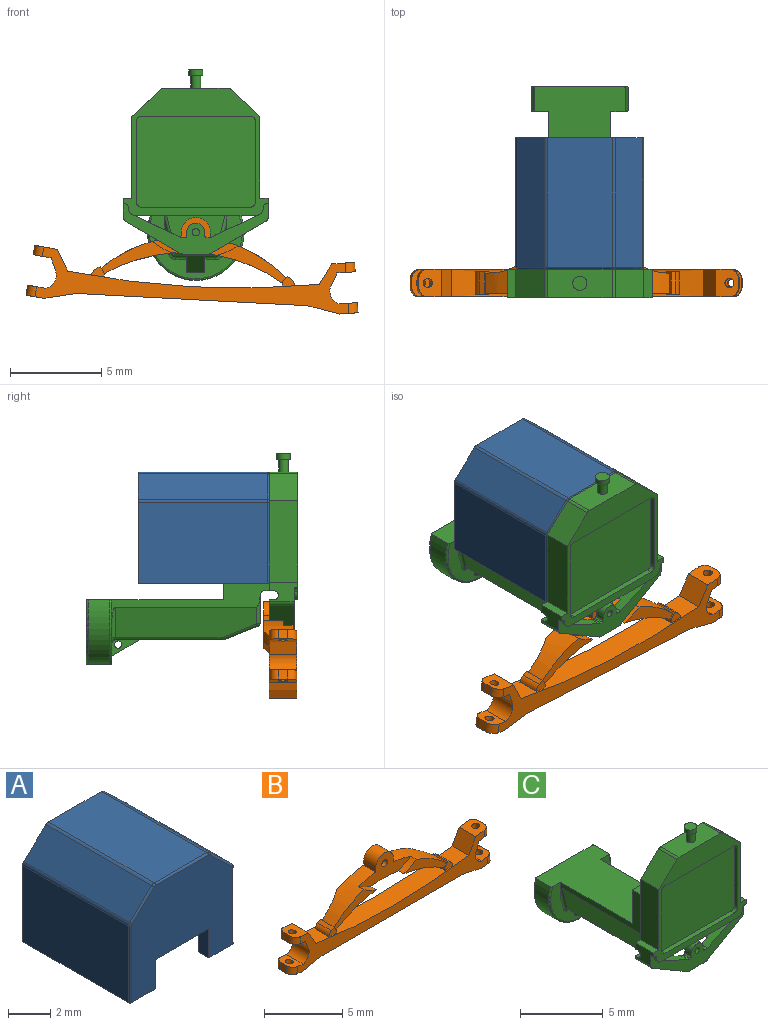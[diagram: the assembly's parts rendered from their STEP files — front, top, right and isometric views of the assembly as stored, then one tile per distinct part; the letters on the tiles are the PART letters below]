
ASSEMBLY  parts=3 mates=4
PART A: 31 faces, bbox 7x7.2x6.1 mm
  f0: plane 7.1x4.44mm, normal (-1,0,0), area 31.5mm2, adj f2,f17,f21,f22
  f1: plane 7.1x4.44mm, normal (1,0,0), area 31.5mm2, adj f2,f16,f18,f30
  f2: plane 7x6.1mm, normal (0,1,0), area 12.1mm2, adj f0,f1,f7,f8,f10,f11,f12,f13
  f3: plane 1.7x0.7mm, normal (1,0,0), area 1.2mm2, adj f5,f6,f9,f17
  f4: plane 1.7x0.7mm, normal (-1,0,0), area 1.2mm2, adj f5,f6,f9,f16
  f5: plane 6.8x6mm, normal (0,-1,0), area 32.3mm2, adj f3,f4,f9,f16,f17,f22,f23,f24
  f6: plane 5.5x5.35mm, normal (0,1,0), area 22mm2, adj f3,f4,f7,f8,f9,f13,f14,f15
  f7: plane 6.5x4.23mm, normal (1,0,0), area 27.5mm2, adj f2,f6,f13,f17
  f8: plane 6.5x4.23mm, normal (-1,0,0), area 27.5mm2, adj f2,f6,f15,f16
  f9: plane 3.6x0.7mm, normal (0,0,-1), area 2.5mm2, adj f3,f4,f5,f6
  f10: plane 7.1x1.48mm, normal (0.69,0,0.72), area 14.5mm2, adj f2,f18,f19,f28
  f11: plane 7.1x3.54mm, normal (0,0,1), area 25.1mm2, adj f2,f19,f20,f26
  f12: plane 7.1x1.48mm, normal (-0.69,0,0.72), area 14.5mm2, adj f2,f20,f21,f24
  f13: plane 6.5x1.18mm, normal (0.69,0,-0.72), area 10.6mm2, adj f2,f6,f7,f14
  f14: plane 6.5x3.14mm, normal (0,0,-1), area 20.4mm2, adj f2,f6,f13,f15
  f15: plane 6.5x1.18mm, normal (-0.69,0,-0.72), area 10.6mm2, adj f2,f6,f8,f14
  f16: plane 7.2x1.7mm, normal (0,0,-1), area 6.1mm2, adj f1,f2,f4,f5,f6,f8,f30
  f17: plane 7.2x1.7mm, normal (0,0,-1), area 6.1mm2, adj f0,f2,f3,f5,f6,f7,f22
  f18: cylinder r=0.25mm len=7.1mm, axis (0,-1,0), area 1.4mm2, adj f1,f2,f10,f29
  f19: cylinder r=0.25mm len=7.1mm, axis (0,1,0), area 1.3mm2, adj f2,f10,f11,f27
  f20: cylinder r=0.25mm len=7.1mm, axis (0,1,0), area 1.3mm2, adj f2,f11,f12,f25
  f21: cylinder r=0.25mm len=7.1mm, axis (0,1,0), area 1.4mm2, adj f0,f2,f12,f23
  f22: cylinder r=0.1mm len=4.44mm, axis (0,0,1), area 0.7mm2, adj f0,f5,f17,f23
  f23: torus R=0.15mm, axis (0,-1,0), area 0mm2, adj f5,f21,f22,f24
  f24: cylinder r=0.1mm len=1.55mm, axis (0.72,0,0.69), area 0.3mm2, adj f5,f12,f23,f25
  f25: torus R=0.15mm, axis (0,-1,0), area 0mm2, adj f5,f20,f24,f26
  f26: cylinder r=0.1mm len=3.54mm, axis (1,0,0), area 0.6mm2, adj f5,f11,f25,f27
  f27: torus R=0.15mm, axis (0,-1,0), area 0mm2, adj f5,f19,f26,f28
  f28: cylinder r=0.1mm len=1.55mm, axis (0.72,0,-0.69), area 0.3mm2, adj f5,f10,f27,f29
  f29: torus R=0.15mm, axis (0,-1,0), area 0mm2, adj f5,f18,f28,f30
  f30: cylinder r=0.1mm len=4.44mm, axis (0,0,-1), area 0.7mm2, adj f1,f5,f16,f29
PART B: 69 faces, bbox 18.2x1.8x4.9 mm
  f0: plane 0.45x0.31mm, normal (0,1,0), area 0.1mm2, adj f6,f46,f51,f59
  f1: plane 1.1x0.29mm, normal (1,0,0), area 0.3mm2, adj f5,f6,f56,f57
  f2: plane 1.1x0.29mm, normal (-1,0,0), area 0.3mm2, adj f3,f5,f56,f57
  f3: cylinder r=7.46mm len=4.27mm, axis (0,1,0), area 6mm2, adj f2,f4,f42,f53,f55,f56,f57,f60
  f4: plane 3.82x1.9mm, normal (0,-1,0), area 2.1mm2, adj f3,f42,f51,f55
  f5: cylinder r=0.8mm len=1.6mm, axis (0,1,0), area 2.8mm2, adj f1,f2,f56,f57
  f6: cylinder r=7.46mm len=4.27mm, axis (0,1,0), area 6mm2, adj f0,f1,f46,f52,f54,f56,f57,f59
  f7: cylinder r=47.86mm len=13.8mm, axis (0,1,0), area 19mm2, adj f10,f11,f16,f26,f40,f41,f43,f44
  f8: plane 0.51x0.5mm, normal (-0.99,0,0.12), area 0.3mm2, adj f17,f28,f30,f32
  f9: plane 0.51x0.5mm, normal (0.99,0,0.12), area 0.3mm2, adj f12,f14,f25,f35
  f10: plane 17.24x2.81mm, normal (0,-1,0), area 16.8mm2, adj f7,f14,f15,f16,f17,f19,f20,f21
  f11: plane 17.24x2.81mm, normal (0,1,0), area 16.6mm2, adj f7,f12,f13,f16,f17,f19,f20,f21
  f12: cylinder r=0.5mm len=0.57mm, axis (-0.12,0,0.99), area 0.4mm2, adj f9,f11,f25,f35
  f13: cylinder r=0.5mm len=0.61mm, axis (-0.12,0,-0.99), area 0.4mm2, adj f11,f18,f19,f33
  f14: cylinder r=0.5mm len=0.57mm, axis (0.12,0,-0.99), area 0.4mm2, adj f9,f10,f25,f35
  f15: cylinder r=0.5mm len=0.61mm, axis (0.12,0,0.99), area 0.4mm2, adj f10,f18,f19,f33
  f16: plane 1.5x1.16mm, normal (0.88,0,0.48), area 2mm2, adj f7,f10,f11,f17
  f17: plane 1.5x1.24mm, normal (0.12,0,0.99), area 1.6mm2, adj f8,f10,f11,f16,f28,f30,f62
  f18: plane 0.55x0.5mm, normal (-0.99,0,0.12), area 0.3mm2, adj f13,f15,f19,f33
  f19: plane 1.5x0.99mm, normal (-0.12,0,-0.99), area 1.2mm2, adj f10,f11,f13,f15,f18,f20,f61
  f20: plane 1.78x1.5mm, normal (0.2,0,-0.98), area 2.7mm2, adj f10,f11,f19,f21
  f21: plane 12.7x1.5mm, normal (0,0,-1), area 19mm2, adj f10,f11,f20,f22
  f22: plane 1.78x1.5mm, normal (-0.2,0,-0.98), area 2.7mm2, adj f10,f11,f21,f23
  f23: plane 1.5x0.99mm, normal (0.12,0,-0.99), area 1.2mm2, adj f10,f11,f22,f24,f27,f29,f63
  f24: plane 0.55x0.5mm, normal (0.99,0,0.12), area 0.3mm2, adj f23,f27,f29,f36
  f25: plane 1.5x1.24mm, normal (-0.12,0,0.99), area 1.6mm2, adj f9,f10,f11,f12,f14,f26,f64
  f26: plane 1.5x1.16mm, normal (-0.88,0,0.48), area 2mm2, adj f7,f10,f11,f25
  f27: cylinder r=0.5mm len=0.61mm, axis (-0.12,0,0.99), area 0.4mm2, adj f11,f23,f24,f36
  f28: cylinder r=0.5mm len=0.57mm, axis (-0.12,0,-0.99), area 0.4mm2, adj f8,f11,f17,f32
  f29: cylinder r=0.5mm len=0.61mm, axis (0.12,0,-0.99), area 0.4mm2, adj f10,f23,f24,f36
  f30: cylinder r=0.5mm len=0.57mm, axis (0.12,0,0.99), area 0.4mm2, adj f8,f10,f17,f32
  f31: plane 1.5x0.68mm, normal (-0.93,0,-0.38), area 1.1mm2, adj f10,f11,f32,f37
  f32: plane 1.5x0.99mm, normal (-0.12,0,-0.99), area 1.2mm2, adj f8,f10,f11,f28,f30,f31,f62
  f33: plane 1.5x0.99mm, normal (0.12,0,0.99), area 1.2mm2, adj f10,f11,f13,f15,f18,f37,f61
  f34: plane 1.5x0.68mm, normal (0.93,0,-0.38), area 1.1mm2, adj f10,f11,f35,f38
  f35: plane 1.5x0.99mm, normal (0.12,0,-0.99), area 1.2mm2, adj f9,f10,f11,f12,f14,f34,f64
  f36: plane 1.5x0.99mm, normal (-0.12,0,0.99), area 1.2mm2, adj f10,f11,f24,f27,f29,f38,f63
  f37: cylinder r=0.75mm len=1.5mm, axis (0,-1,0), area 1.9mm2, adj f10,f11,f31,f33
  f38: cylinder r=0.75mm len=1.5mm, axis (0,-1,0), area 1.9mm2, adj f10,f11,f34,f36
  f39: plane 1.25x0.25mm, normal (-0.55,0,0.83), area 0.4mm2, adj f40,f42,f43,f44
  f40: cylinder r=0.5mm len=1.25mm, axis (0,1,0), area 0.5mm2, adj f7,f39,f43,f44
  f41: plane 1.25x0.22mm, normal (0.99,0,-0.11), area 0.3mm2, adj f7,f42,f43,f44,f51
  f42: plane 1.25x0.38mm, normal (0.83,0,0.55), area 0.2mm2, adj f3,f4,f39,f41,f43,f44,f53
  f43: plane 0.72x0.6mm, normal (0,-1,0), area 0.3mm2, adj f7,f39,f40,f41,f42
  f44: plane 0.72x0.6mm, normal (0,1,0), area 0.3mm2, adj f7,f39,f40,f41,f42
  f45: plane 1.25x0.25mm, normal (0.55,0,0.83), area 0.4mm2, adj f46,f48,f49,f50
  f46: plane 1.25x0.38mm, normal (-0.83,0,0.55), area 0.2mm2, adj f0,f6,f45,f47,f49,f50,f52
  f47: plane 1.25x0.22mm, normal (-0.99,0,-0.11), area 0.3mm2, adj f7,f46,f49,f50,f51
  f48: cylinder r=0.5mm len=1.25mm, axis (0,1,0), area 0.5mm2, adj f7,f45,f49,f50
  f49: plane 0.72x0.6mm, normal (0,-1,0), area 0.3mm2, adj f7,f45,f46,f47,f48
  f50: plane 0.72x0.6mm, normal (0,1,0), area 0.3mm2, adj f7,f45,f46,f47,f48
  f51: cylinder r=9.12mm len=9.75mm, axis (0,1,0), area 13.8mm2, adj f0,f4,f41,f47,f52,f53,f54,f55
  f52: plane 3.82x1.9mm, normal (0,-1,0), area 2.1mm2, adj f6,f46,f51,f54
  f53: plane 0.45x0.31mm, normal (0,1,0), area 0.1mm2, adj f3,f42,f51,f60
  f54: cylinder r=4mm len=1.11mm, axis (0,-1,0), area 0.6mm2, adj f6,f51,f52,f56
  f55: cylinder r=4mm len=1.11mm, axis (0,-1,0), area 0.6mm2, adj f3,f4,f51,f56
  f56: plane 4.71x2mm, normal (0,-1,0), area 4.4mm2, adj f1,f2,f3,f5,f6,f51,f54,f55
  f57: plane 6.45x2.42mm, normal (0,1,0), area 6.4mm2, adj f1,f2,f3,f5,f6,f51,f58,f59
  f58: cylinder r=0.25mm len=1.1mm, axis (0,-1,0), area 1.7mm2, adj f56,f57
  f59: cylinder r=4mm len=2.12mm, axis (-0.33,0,-0.94), area 1.1mm2, adj f0,f6,f51,f57
  f60: cylinder r=4mm len=2.12mm, axis (0.33,0,-0.94), area 1.1mm2, adj f3,f51,f53,f57
  f61: cylinder r=0.25mm len=0.61mm, axis (0.12,0,0.99), area 0.9mm2, adj f19,f33
  f62: cylinder r=0.25mm len=0.57mm, axis (0.12,0,0.99), area 0.8mm2, adj f17,f32
  f63: cylinder r=0.25mm len=0.61mm, axis (-0.12,0,0.99), area 0.9mm2, adj f23,f36
  f64: cylinder r=0.25mm len=0.57mm, axis (-0.12,0,0.99), area 0.8mm2, adj f25,f35
  f65: cylinder r=0.2mm len=1mm, axis (0,1,0), area 1.3mm2, adj f11,f66
  f66: plane 0.4x0.4mm, normal (0,1,0), area 0.1mm2, adj f65
  f67: cylinder r=0.2mm len=1mm, axis (0,1,0), area 1.3mm2, adj f11,f68
  f68: plane 0.4x0.4mm, normal (0,1,0), area 0.1mm2, adj f67
PART C: 115 faces, bbox 8x11.6x11.8 mm
  f0: plane 5.1x3.45mm, normal (0,-1,0), area 6.2mm2, adj f6,f7,f62,f81,f83,f84,f85,f94
  f1: plane 7.94x6.5mm, normal (0,1,0), area 36.6mm2, adj f3,f4,f6,f7,f10,f23,f24,f25
  f2: plane 2.57x1.14mm, normal (0,1,0), area 1.2mm2, adj f4,f12,f47,f52,f54,f68,f72,f107
  f3: plane 1.56x1.06mm, normal (1,0,0), area 1.3mm2, adj f1,f11,f20,f28,f44,f50,f69,f71
  f4: plane 1.56x1.06mm, normal (-1,0,0), area 1.3mm2, adj f1,f2,f19,f28,f45,f50,f69,f70
  f5: plane 6.5x0.99mm, normal (0,0,-1), area 6mm2, adj f9,f28,f46,f56,f57,f75,f77
  f6: plane 8.65x3.74mm, normal (1,0,0), area 9.3mm2, adj f0,f1,f10,f59,f62,f63,f69,f74
  f7: plane 8.65x3.74mm, normal (-1,0,0), area 9.3mm2, adj f0,f1,f10,f61,f62,f63,f69,f74
  f8: plane 2.41x1.36mm, normal (-0.42,0,0.91), area 3.1mm2, adj f11,f50,f53,f55,f67,f111
  f9: cylinder r=0.45mm len=0.99mm, axis (0,-1,0), area 0.2mm2, adj f5,f22,f28,f50,f67,f76
  f10: plane 3.4x2.5mm, normal (0,0,1), area 8.5mm2, adj f1,f6,f7,f63
  f11: plane 2.57x1.14mm, normal (0,1,0), area 1.2mm2, adj f3,f8,f49,f51,f55,f67,f73,f108
  f12: plane 2.41x1.36mm, normal (0.42,0,0.91), area 3.1mm2, adj f2,f50,f53,f54,f68,f112
  f13: cylinder r=0.5mm len=1mm, axis (0,-1,0), area 0.9mm2, adj f17,f18,f50,f53
  f14: cylinder r=0.2mm len=0.56mm, axis (0,-1,0), area 0.7mm2, adj f50,f53
  f15: plane 0.56x0.09mm, normal (0,0,1), area 0.1mm2, adj f50,f53,f112,f113
  f16: plane 0.56x0.09mm, normal (0,0,1), area 0.1mm2, adj f50,f53,f111,f114
  f17: plane 0.56x0.2mm, normal (-1,0,0), area 0.1mm2, adj f13,f50,f53,f113
  f18: plane 0.56x0.2mm, normal (1,0,0), area 0.1mm2, adj f13,f50,f53,f114
  f19: plane 0.2x0.05mm, normal (0,0,-1), area 0mm2, adj f4,f21,f28,f50
  f20: plane 0.2x0.05mm, normal (0,0,-1), area 0mm2, adj f3,f22,f28,f50
  f21: cylinder r=0.22mm len=0.22mm, axis (0,-1,0), area 0.1mm2, adj f19,f28,f46,f50
  f22: cylinder r=0.22mm len=0.22mm, axis (0,-1,0), area 0.1mm2, adj f9,f20,f28,f50
  f23: plane 4.48x1.56mm, normal (-1,0,0), area 7mm2, adj f1,f27,f28,f45
  f24: plane 4.48x1.56mm, normal (1,0,0), area 7mm2, adj f1,f25,f28,f44
  f25: plane 1.56x1.56mm, normal (0.69,0,0.72), area 3.4mm2, adj f1,f24,f28,f42
  f26: plane 3.54x1.56mm, normal (0,0,1), area 5.3mm2, adj f1,f28,f38,f42,f43
  f27: plane 1.56x1.56mm, normal (-0.69,0,0.72), area 3.4mm2, adj f1,f23,f28,f43
  f28: plane 7.94x7mm, normal (0,-1,0), area 14.3mm2, adj f3,f4,f5,f9,f19,f20,f21,f22
  f29: plane 4.4x0.3mm, normal (1,0,0), area 1.3mm2, adj f28,f33,f34,f37
  f30: plane 5.94x0.3mm, normal (0,0,1), area 1.8mm2, adj f28,f33,f34,f35
  f31: plane 4.4x0.3mm, normal (-1,0,0), area 1.3mm2, adj f28,f33,f35,f36
  f32: plane 5.94x0.3mm, normal (0,0,-1), area 1.8mm2, adj f28,f33,f36,f37
  f33: plane 6.54x5mm, normal (0,-1,0), area 32.6mm2, adj f29,f30,f31,f32,f34,f35,f36,f37
  f34: cylinder r=0.3mm len=0.3mm, axis (0,1,0), area 0.1mm2, adj f28,f29,f30,f33
  f35: cylinder r=0.3mm len=0.3mm, axis (0,-1,0), area 0.1mm2, adj f28,f30,f31,f33
  f36: cylinder r=0.3mm len=0.3mm, axis (0,1,0), area 0.1mm2, adj f28,f31,f32,f33
  f37: cylinder r=0.3mm len=0.3mm, axis (0,-1,0), area 0.1mm2, adj f28,f29,f32,f33
  f38: cylinder r=0.28mm len=0.7mm, axis (0,0,-1), area 1.2mm2, adj f26,f41
  f39: cylinder r=0.39mm len=0.78mm, axis (0,0,-1), area 0.7mm2, adj f40,f41
  f40: plane 0.78x0.78mm, normal (0,0,1), area 0.5mm2, adj f39
  f41: plane 0.78x0.78mm, normal (0,0,-1), area 0.2mm2, adj f38,f39
  f42: cylinder r=0.25mm len=1.56mm, axis (0,1,0), area 0.3mm2, adj f1,f25,f26,f28
  f43: cylinder r=0.25mm len=1.56mm, axis (0,1,0), area 0.3mm2, adj f1,f26,f27,f28
  f44: plane 1.56x0.47mm, normal (0,0,1), area 0.7mm2, adj f1,f3,f24,f28
  f45: plane 1.56x0.47mm, normal (0,0,1), area 0.7mm2, adj f1,f4,f23,f28
  f46: cylinder r=0.45mm len=0.99mm, axis (0,-1,0), area 0.2mm2, adj f5,f21,f28,f50,f68,f78
  f47: plane 2.97x1.74mm, normal (-0.51,0,-0.86), area 3.3mm2, adj f2,f50,f52,f53,f107,f109
  f48: plane 1.34x0.56mm, normal (0,0,-1), area 0.8mm2, adj f50,f53,f109,f110
  f49: plane 2.97x1.74mm, normal (0.51,0,-0.86), area 3.3mm2, adj f11,f50,f51,f53,f108,f110
  f50: plane 7.94x2.77mm, normal (0,-1,0), area 6.7mm2, adj f3,f4,f8,f9,f12,f13,f14,f15
  f51: cylinder r=10mm len=1.01mm, axis (0,1,0), area 0.8mm2, adj f11,f49,f53,f55
  f52: cylinder r=10mm len=1.01mm, axis (0,1,0), area 0.8mm2, adj f2,f47,f53,f54
  f53: plane 4.82x1.7mm, normal (0,1,0), area 3.9mm2, adj f8,f12,f13,f14,f15,f16,f17,f18
  f54: cylinder r=1.4mm len=0.8mm, axis (0,1,0), area 0mm2, adj f2,f12,f52,f53
  f55: cylinder r=1.4mm len=0.8mm, axis (0,1,0), area 0mm2, adj f8,f11,f51,f53
  f56: plane 2.14x0.5mm, normal (0,1,0), area 0.7mm2, adj f5,f57
  f57: cylinder r=1.4mm len=2.14mm, axis (0,1,0), area 1mm2, adj f5,f56,f70,f71,f75,f77
  f58: plane 3.31x1.51mm, normal (0,-1,0), area 4.3mm2, adj f64,f74,f87,f90,f99
  f59: plane 7.74x1.65mm, normal (0.97,0,-0.24), area 12.5mm2, adj f6,f99,f101,f103,f104
  f60: plane 5.9x2.19mm, normal (0,0,-1), area 11.6mm2, adj f81,f83,f84,f88,f95,f97,f103,f106
  f61: plane 7.74x1.65mm, normal (-0.97,0,-0.24), area 12.5mm2, adj f7,f90,f92,f94,f95
  f62: plane 7.56x5mm, normal (0,0,1), area 27.8mm2, adj f0,f6,f7,f63,f79,f80,f85,f86
  f63: plane 3.4x2.5mm, normal (0,1,0), area 8.5mm2, adj f6,f7,f10,f62
  f64: cylinder r=0.2mm len=5mm, axis (0,-1,0), area 6.3mm2, adj f58,f65
  f65: plane 0.4x0.4mm, normal (0,-1,0), area 0.1mm2, adj f64
  f66: plane 2.56x1.84mm, normal (0,-0.37,-0.93), area 4.7mm2, adj f87,f88,f92,f101
  f67: plane 1.37x0.19mm, normal (-1,0,0), area 0.1mm2, adj f8,f9,f11,f50,f71,f73,f76
  f68: plane 1.37x0.19mm, normal (1,0,0), area 0.1mm2, adj f2,f12,f46,f50,f70,f72,f78
  f69: plane 7.94x0.5mm, normal (0,0,-1), area 2.8mm2, adj f1,f3,f4,f6,f7,f70,f71,f74
  f70: cylinder r=0.25mm len=3.97mm, axis (1,0,0), area 1.9mm2, adj f4,f57,f68,f69,f72,f77,f78
  f71: cylinder r=0.25mm len=3.97mm, axis (1,0,0), area 1.9mm2, adj f3,f57,f67,f69,f73,f75,f76
  f72: plane 0.7x0.25mm, normal (0,0,1), area 0.2mm2, adj f2,f4,f68,f70
  f73: plane 0.7x0.25mm, normal (0,0,1), area 0.2mm2, adj f3,f11,f67,f71
  f74: cylinder r=0.25mm len=3.4mm, axis (1,0,0), area 1.3mm2, adj f6,f7,f58,f69,f89,f98
  f75: cylinder r=0.1mm len=2.32mm, axis (1,0,0), area 0.5mm2, adj f5,f57,f71,f76
  f76: bspline ~0.22x0.16mm, area 0mm2, adj f9,f67,f71,f75
  f77: cylinder r=0.1mm len=2.32mm, axis (1,0,0), area 0.5mm2, adj f5,f57,f70,f78
  f78: bspline ~0.22x0.16mm, area 0mm2, adj f46,f68,f70,f77
  f79: cylinder r=2.65mm len=5.3mm, axis (0,-1,0), area 12.2mm2, adj f62,f85,f86
  f80: plane 5.1x3.45mm, normal (0,1,0), area 14.7mm2, adj f62,f86
  f81: plane 1.5x1mm, normal (0,-0.51,-0.86), area 1.7mm2, adj f0,f60,f83,f84
  f82: cylinder r=0.2mm len=1mm, axis (-1,0,0), area 1.3mm2, adj f83,f84
  f83: plane 1.5x0.9mm, normal (1,0,0), area 0.5mm2, adj f0,f60,f81,f82,f106
  f84: plane 1.5x0.9mm, normal (-1,0,0), area 0.5mm2, adj f0,f60,f81,f82,f97
  f85: torus R=2.55mm, axis (0,-1,0), area 1.6mm2, adj f0,f62,f79
  f86: torus R=2.55mm, axis (0,-1,0), area 1.6mm2, adj f62,f79,f80
  f87: cylinder r=0.2mm len=2.56mm, axis (1,0,0), area 0.6mm2, adj f58,f66,f91,f100
  f88: cylinder r=0.2mm len=2.19mm, axis (-1,0,0), area 0.2mm2, adj f60,f66,f93,f102
  f89: bspline ~0.26x0.26mm, area 0mm2, adj f7,f74,f90
  f90: cylinder r=0.2mm len=1.56mm, axis (-0.24,0,0.97), area 0.4mm2, adj f7,f58,f61,f89,f91
  f91: sphere r=0.2mm, area 0mm2, adj f87,f90,f92
  f92: cylinder r=0.2mm len=1.91mm, axis (-0.09,-0.92,0.37), area 0.5mm2, adj f61,f66,f91,f93
  f93: sphere r=0.2mm, area 0mm2, adj f88,f92,f95
  f94: cylinder r=0.2mm len=1.7mm, axis (0.24,0,-0.97), area 0.4mm2, adj f0,f7,f61,f96
  f95: cylinder r=0.2mm len=5.9mm, axis (0,-1,0), area 1.6mm2, adj f60,f61,f93,f96
  f96: torus R=0.4mm, axis (0,-1,0), area 0.1mm2, adj f0,f94,f95,f97
  f97: cylinder r=0.2mm len=0.59mm, axis (1,0,0), area 0.2mm2, adj f0,f60,f84,f96
  f98: bspline ~0.26x0.26mm, area 0mm2, adj f6,f74,f99
  f99: cylinder r=0.2mm len=1.56mm, axis (-0.24,0,-0.97), area 0.4mm2, adj f6,f58,f59,f98,f100
  f100: sphere r=0.2mm, area 0mm2, adj f87,f99,f101
  f101: cylinder r=0.2mm len=1.91mm, axis (-0.09,0.92,-0.37), area 0.5mm2, adj f59,f66,f100,f102
  f102: sphere r=0.2mm, area 0mm2, adj f88,f101,f103
  f103: cylinder r=0.2mm len=5.9mm, axis (0,-1,0), area 1.6mm2, adj f59,f60,f102,f105
  f104: cylinder r=0.2mm len=1.7mm, axis (0.24,0,0.97), area 0.4mm2, adj f0,f6,f59,f105
  f105: torus R=0.4mm, axis (0,-1,0), area 0.1mm2, adj f0,f103,f104,f106
  f106: cylinder r=0.2mm len=0.59mm, axis (1,0,0), area 0.2mm2, adj f0,f60,f83,f105
  f107: cylinder r=0.25mm len=1.36mm, axis (0,-1,0), area 0.4mm2, adj f2,f4,f47,f50
  f108: cylinder r=0.25mm len=1.36mm, axis (0,1,0), area 0.4mm2, adj f3,f11,f49,f50
  f109: cylinder r=0.4mm len=0.56mm, axis (0,-1,0), area 0.1mm2, adj f47,f48,f50,f53
  f110: cylinder r=0.4mm len=0.56mm, axis (0,-1,0), area 0.1mm2, adj f48,f49,f50,f53
  f111: cylinder r=0.4mm len=0.56mm, axis (0,1,0), area 0.1mm2, adj f8,f16,f50,f53
  f112: cylinder r=0.4mm len=0.56mm, axis (0,1,0), area 0.1mm2, adj f12,f15,f50,f53
  f113: cylinder r=0.1mm len=0.56mm, axis (0,-1,0), area 0.1mm2, adj f15,f17,f50,f53
  f114: cylinder r=0.1mm len=0.56mm, axis (0,1,0), area 0.1mm2, adj f16,f18,f50,f53
PLACE A t=(0,8.76,-4.98)mm
PLACE B rot(axis=(0,1,0),3deg) t=(-0.13,0.81,-7.48)mm
PLACE C t=(0,1.56,-4.98)mm
MATE planar A.f11 <-> C.f38  axis (0,0,1) through (0,5.21,2.92)mm
MATE revolute B.f5 <-> C.f13  axis (0,-1,0) through (0,0.76,-4.98)mm
MATE planar C.f23 <-> A.f0  axis (-1,0,0) through (-3.5,0.78,-0.87)mm
MATE planar C.f1 <-> A.f5  axis (0,1,0) through (0,1.56,-0.14)mm
